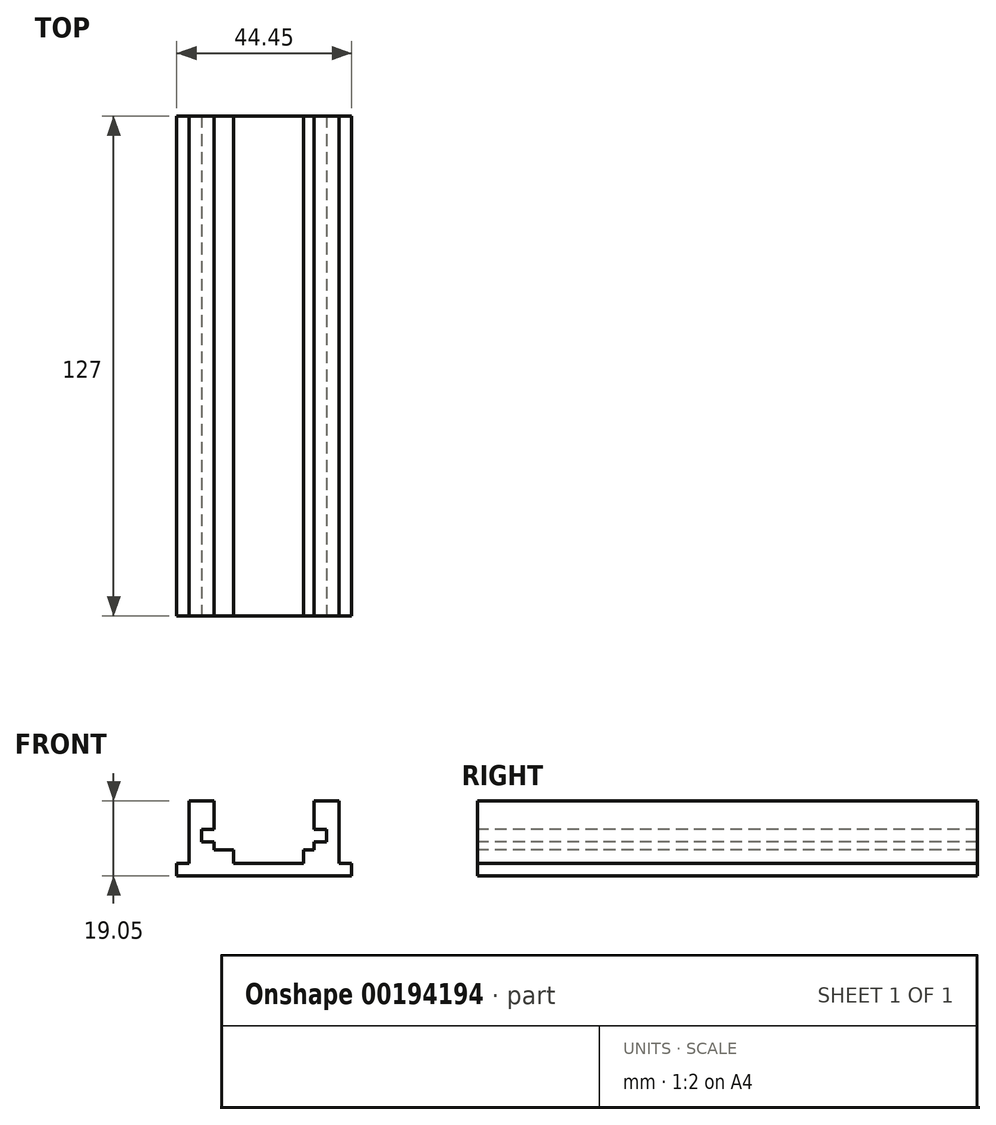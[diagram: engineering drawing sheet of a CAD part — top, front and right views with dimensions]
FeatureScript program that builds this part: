
annotation { "Feature Type Name" : "Feature", "Feature Type Description" : "" }
export const myFeature = defineFeature(function(context is Context, id is Id, definition is map)
    precondition{}
    {
        {
            var Q0;
            Q0=qCreatedBy(makeId("Front.planeOp"),FACE);
            var sketch = newSketch(context, id + "F0", { "sketchPlane" : qUnion([Q0])});
            skLineSegment(sketch, "E0", {"start": v(17.9, 0) * mm, "end": v(-23.37, 0) * mm});
            skLineSegment(sketch, "E1", {"start": v(-23.37, 0) * mm, "end": v(-23.37, 3.17) * mm});
            skLineSegment(sketch, "E2", {"start": v(-23.37, 3.17) * mm, "end": v(-20.2, 3.17) * mm});
            skLineSegment(sketch, "E3", {"start": v(-20.2, 3.18) * mm, "end": v(-20.2, 19.05) * mm});
            skLineSegment(sketch, "E4", {"start": v(-20.2, 19.05) * mm, "end": v(-13.84, 19.05) * mm});
            skLineSegment(sketch, "E5", {"start": v(-13.84, 19.05) * mm, "end": v(-13.84, 11.75) * mm});
            skLineSegment(sketch, "E6", {"start": v(-13.84, 11.75) * mm, "end": v(-17.02, 11.75) * mm});
            skLineSegment(sketch, "E7", {"start": v(-17.02, 11.75) * mm, "end": v(-17.02, 8.57) * mm});
            skLineSegment(sketch, "E8", {"start": v(-17.02, 8.57) * mm, "end": v(-13.84, 8.57) * mm});
            skLineSegment(sketch, "E9", {"start": v(-13.84, 8.57) * mm, "end": v(-13.84, 6.6) * mm});
            skLineSegment(sketch, "E10", {"start": v(-13.84, 6.6) * mm, "end": v(-8.9, 6.6) * mm});
            skLineSegment(sketch, "E11", {"start": v(-8.9, 6.6) * mm, "end": v(-8.9, 3.17) * mm});
            skLineSegment(sketch, "E12", {"start": v(-8.9, 3.17) * mm, "end": v(8.9, 3.18) * mm});
            skLineSegment(sketch, "E13", {"start": v(8.9, 3.18) * mm, "end": v(8.9, 6.6) * mm});
            skLineSegment(sketch, "E14", {"start": v(8.9, 6.6) * mm, "end": v(11.56, 6.6) * mm});
            skLineSegment(sketch, "E15", {"start": v(11.56, 6.6) * mm, "end": v(11.56, 8.57) * mm});
            skLineSegment(sketch, "E16", {"start": v(11.56, 8.57) * mm, "end": v(14.73, 8.57) * mm});
            skLineSegment(sketch, "E17", {"start": v(14.73, 8.57) * mm, "end": v(14.73, 11.75) * mm});
            skLineSegment(sketch, "E18", {"start": v(14.73, 11.75) * mm, "end": v(11.56, 11.75) * mm});
            skLineSegment(sketch, "E19", {"start": v(11.56, 11.75) * mm, "end": v(11.56, 19.05) * mm});
            skLineSegment(sketch, "E20", {"start": v(11.56, 19.05) * mm, "end": v(17.9, 19.05) * mm});
            skLineSegment(sketch, "E21", {"start": v(17.9, 19.05) * mm, "end": v(17.9, 3.18) * mm});
            skLineSegment(sketch, "E22", {"start": v(17.9, 3.18) * mm, "end": v(21.08, 3.18) * mm});
            skLineSegment(sketch, "E23", {"start": v(21.08, 3.18) * mm, "end": v(21.08, 0) * mm});
            skLineSegment(sketch, "E24", {"start": v(21.08, 0) * mm, "end": v(17.9, 0) * mm});
            skSolve(sketch);
        }
        {
            var Q0;
            Q0=makeQuery(id+"F0.imprint","IMPRINT",FACE,{"disambiguationData":[TD([[makeQuery(id+"F0.imprint","IMPRINT",EDGE,{"derivedFrom":sQuery(id+"F0.wireOp",EDGE,"E0")}),-1.0]])]});
            extrude(context, id + "F1", {"entities" : qUnion([Q0]), "oppositeDirection" : true, "depth" : 127 * mm});
        }
    });
